# Revit family: Zumtobel RESCLITE PRO MSC
name_source: partatom
category: Lighting Fixtures
revit_build: Autodesk Revit 2016 (Build: 20150220_1215(x64)
units: mm (PartAtom-declared; Revit-internal decimal feet)

## family parameters
Cut with Voids When Loaded = No
Host = Face
Light Source = Yes
OmniClass Number = 23.80.70.11
OmniClass Title = Luminaries for Internal Lighting
Part Type = Normal
Room Calculation Point = No
Round Connector Dimension = Use Diameter
Shared = No

## types (7) — shared parameters
Assembly Code = D5020200
Body = Zumtobel_Metal_White
Color Filter = 16777215
Description = LED Safety luminaire
Dimming Lamp Color Temperature Shift = <None>
Lamp = LED
Length = 146 mm  [stored 0.479003 ft]
MSC ANT HP = Yes
Manufacturer = Zumtobel Lighting
Tilt Angle = 180.00°
URL = http://www.zumtobel.com
Voltage = 230 V
Width = 146 mm  [stored 0.479003 ft]
zero-valued in all types: Default Elevation

## per-type parameters (varying)
| type | Apparent Load | Height | MSC | MSC ESC | Model | Offset | Photometric Web File |
| RESCLITE PRO MSC ANT HP | 8 VA | 46 mm  [stored 0.150919 ft] | Yes | No | 42185731 | 15 mm | 42185731_(STD_LEO).IES |
| RESCLITE PRO MSC ANT | 5 VA | 35 mm  [stored 0.114829 ft] | Yes | No | 42185709 | 0 mm  [stored 0 ft] | 42185709_(STD_LEO).IES |
| RESCLITE PRO MSC ESC | 5 VA | 35 mm  [stored 0.114829 ft] | No | Yes | 42185710 | 0 mm  [stored 0 ft] | 42185710_(STD_LEO).IES |
| RESCLITE PRO MSC SPOT | 5 VA | 35 mm  [stored 0.114829 ft] | No | Yes | 42185712 | 0 mm  [stored 0 ft] | 42185712_(STD_LEO).IES |
| RESCLITE PRO MSC ESC90 HP | 8 VA | 48 mm  [stored 0.15748 ft] | No | Yes | 42185733 | 15 mm | 42185733_(STD_LEO).IES |
| RESCLITE PRO MSC ESC90 | 5 VA | 35 mm  [stored 0.114829 ft] | No | Yes | 42185711 | 0 mm  [stored 0 ft] | 42185711_(STD_LEO).IES |
| RESCLITE PRO MSC ESC HP | 8 VA | 48 mm  [stored 0.15748 ft] | No | Yes | 42185732 | 15 mm | 42185732_(STD_LEO).IES |

note: [stored X ft] marks values corroborated as IEEE doubles in the binary element streams (Revit-internal decimal feet)

## geometry (parser evidence)
native form markers: Sweep x1
no freeform markers — native parametric forms only
